annotation { "Feature Type Name" : "Feature", "Feature Type Description" : "" }
export const myFeature = defineFeature(function(context is Context, id is Id, definition is map)
    precondition{}
    {
        {
            var Q0;
            Q0=qCreatedBy(makeId("Top.planeOp"),FACE);
            var sketch = newSketch(context, id + "F0", { "sketchPlane" : qUnion([Q0])});
            skText(sketch, "E0", { "text": "AMY WARMKA", "fontName": "OpenSans-Bold.ttf"});
            const initialGuessF0  = {"E0": [-0.10414, 8e-05, 1, 0, 0.01017]};
            skSetInitialGuess(sketch, initialGuessF0);
            skSolve(sketch);
        }
        {
            var Q0;
            Q0 = qSketchRegion(id + "F0", true);
            extrude(context, id + "F1", {"entities" : qUnion([Q0]), "depth" : 6.35 * mm});
        }
        {
            var Q0;
            Q0=qCreatedBy(makeId("Right.planeOp"),FACE);
            var sketch = newSketch(context, id + "F2", { "sketchPlane" : qUnion([Q0])});
            skLineSegment(sketch, "E1.bottom", {"start": v(-2.09, 0) * mm, "end": v(13.46, 0) * mm});
            skLineSegment(sketch, "E1.top", {"start": v(-2.09, -3.98) * mm, "end": v(13.46, -3.98) * mm});
            skLineSegment(sketch, "E1.left", {"start": v(-2.09, 0) * mm, "end": v(-2.09, -3.98) * mm});
            skLineSegment(sketch, "E1.right", {"start": v(13.46, 0) * mm, "end": v(13.46, -3.98) * mm});
            skSolve(sketch);
        }
        {
            var Q0;
            Q0=makeQuery(id+"F2.imprint","IMPRINT",FACE,{"disambiguationData":[TD([[makeQuery(id+"F2.imprint","IMPRINT",EDGE,{"derivedFrom":sQuery(id+"F2.wireOp",EDGE,"E1.bottom")}),-1.0]])]});
            extrude(context, id + "F3", {"entities" : qUnion([Q0]), "oppositeDirection" : true, "depth" : 109.22 * mm});
        }
    });